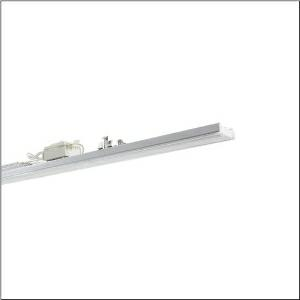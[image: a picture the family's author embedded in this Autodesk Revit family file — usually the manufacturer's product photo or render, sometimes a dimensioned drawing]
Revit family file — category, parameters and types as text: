
# Revit family: licross_r__21_recessed_ho_52tl11cn4c5s_2da8
name_source: partatom
category: Lighting Fixtures
units: mm (PartAtom-declared; Revit-internal decimal feet)

## family parameters
Cut with Voids When Loaded = No
Host = Face
Light Source = No
Part Type = Normal
Room Calculation Point = No
Round Connector Dimension = Use Diameter
Shared = No

## types (1)
- --- (1 x LED, 12640 lm, 68.4 W, 4000K)
    Apparent Load = 68 VA
    CIE Flux Codes = 87 95 99 100 100
    Color Rendering = 80
    Color Temperature = 4000K
    Default Elevation = 1800 mm
    Description = Licross® 21 Recessed HO, luminaire insert, of sheet steel, galvanised, coil coated, white, length: 1.500mm, width: 66mm, height: 67mm, LED rated luminous flux: 12.640lm, light colour: 840, control gear: ON/OFF Multilumen, CLOi, control gear: ECG Multilumen, with plug, 3-pole, with phase selection, mains connection: 220..240V, AC, 50/60Hz, start of lifetime: 68W, end of service life: 83W, halogen-free wiring, primary light control with lens, of plastic, primary optical cover: cover, of PMMA, light emission: direct distribution, primary light characteristic: symmetric, protection rating (complete): IP40, insulation class (complete): insulation class I (protective earthing), certification: CE, ENEC, VDE, UKCA, protection symbol: D if used in an environment without relevant dust loads with corresponding accessories, impact resistance: IK06, permissible ambient temperature for indoor applications: -35..+30°C, corresponds to IFS (International Featured Standards) requirements for safety and quality in the food industry, reducing of maximum allowable ambient temperature of 5°C with ceiling mounting, LABS conformity tested according to VDMA 24364:2018-05, packaging unit: 1 piece
    Height = 58 mm
    Lamp = 1 x LED
    Lamp Light Flux = 12640 lm
    Lamp Power = 68.4 W
    Lamp count = 1
    Length = 1500 mm
    Luminous efficacy = 185 lm/W
    Manufacturer = Siteco
    ModVariant = No
    Model = 52TL11CN4C5S
    Mounting Place = Ceiling
    Mounting Type = Pendant
    Number of Poles = 1
    OnlyDefault = Yes
    Power Factor = 1
    Product Name = Licross® 21 Recessed HO
    Product group = luminaire insert
    ProductGroupID = 902
    Protection Class = Protection class I
    Protection Degree = IP 40
    RLX_Detail_Level = 1
    RLX_Emergency_Light_Flux = 0 lm
    RLX_Emergency_Type = 0
    RLX_Emergency_Type_DB = No
    RlxData = <blob elided: 22325 chars, md5=24bc1549>
    Socket = socket
    Standby Power = 0 W
    System Light Flux = 12640 lm
    System Power = 68 W
    Type Comments = factory setting: luminous flux: 100 % | (A | C | E) | 161 mA
    Type Image = l_1296930.jpg
    URL = http://relux.com
    VarID = @adj_110718
    Voltage = 0 V
    Weight = 0.00 kg
    Width = 66 mm

## geometry (parser evidence)
native form markers: Blend x4, Sweep x9
no freeform markers — native parametric forms only
